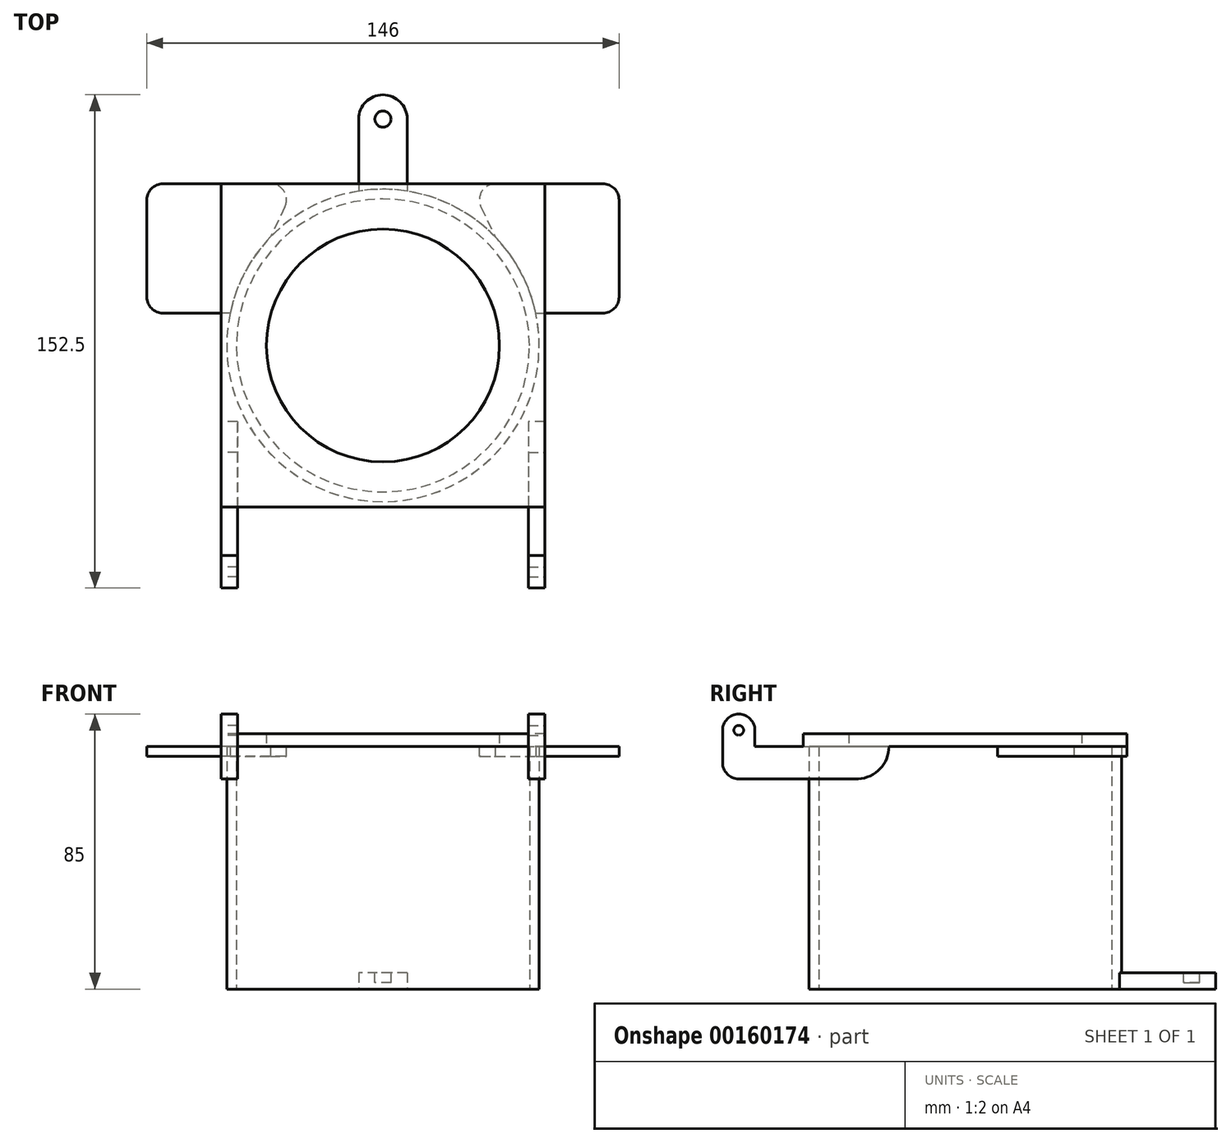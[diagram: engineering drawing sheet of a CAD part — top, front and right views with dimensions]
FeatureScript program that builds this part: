
annotation { "Feature Type Name" : "Feature", "Feature Type Description" : "" }
export const myFeature = defineFeature(function(context is Context, id is Id, definition is map)
    precondition{}
    {
        {
            var Q0;
            Q0=qCreatedBy(makeId("Top.planeOp"),FACE);
            var sketch = newSketch(context, id + "F0", { "sketchPlane" : qUnion([Q0])});
            skCircle(sketch, "E0", {"center": v(0, 0) * mm, "radius": 48.3 * mm});
            skCircle(sketch, "E1", {"center": v(0, 0) * mm, "radius": 45.3 * mm});
            skLineSegment(sketch, "E2.top", {"start": v(7.5, 46.67) * mm, "end": v(-7.5, 46.67) * mm});
            skLineSegment(sketch, "E2.left", {"start": v(7.5, 70) * mm, "end": v(7.5, 46.67) * mm});
            skLineSegment(sketch, "E2.right", {"start": v(-7.5, 70) * mm, "end": v(-7.5, 46.67) * mm});
            skArc(sketch, "E3", {"start": v(-7.5, 70) * mm, "mid": v(0, 77.5) * mm, "end": v(7.5, 70) * mm});
            skSolve(sketch);
        }
        {
            var Q0;
            Q0=makeQuery(id+"F0.imprint","IMPRINT",FACE,{"disambiguationData":[TD([[makeQuery(id+"F0.imprint","IMPRINT",EDGE,{"derivedFrom":sQuery(id+"F0.wireOp",EDGE,"E1")}),-1.0]])]});
            var Q1;
            {var subQ5=sQuery(id+"F0.wireOp",EDGE,"E2.top");Q1=makeQuery(id+"F0.imprint","IMPRINT",FACE,{"disambiguationData":[TD([[makeQuery(id+"F0.imprint","IMPRINT",EDGE,{"derivedFrom":subQ5}),-1.0]])]});}
            extrude(context, id + "F1", {"entities" : qUnion([Q0, Q1]), "depth" : 75 * mm});
        }
        {
            var Q0;
            Q0=qSketchRegion(id+"F0",true);
            extrude(context, id + "F2", {"entities" : qUnion([Q0]), "operationType" : NewBodyOperationType.ADD, "depth" : 5 * mm});
        }
        {
            var Q0;
            Q0=makeQuery(id+"F2.opExtrude","CAP_FACE",FACE,{"disambiguationData":[OSD([sQuery(id+"F0.wireOp",EDGE,"E0"),sQuery(id+"F0.wireOp",EDGE,"E1"),sQuery(id+"F0.wireOp",EDGE,"E2.left"),sQuery(id+"F0.wireOp",EDGE,"E2.right"),sQuery(id+"F0.wireOp",EDGE,"E3")])],"isStart":false});
            var sketch = newSketch(context, id + "F3", { "sketchPlane" : qUnion([Q0])});
            skCircle(sketch, "E4", {"center": v(0, 70) * mm, "radius": 2.5 * mm});
            skSolve(sketch);
        }
        {
            var Q0;
            Q0=makeQuery(id+"F3.imprint","IMPRINT",FACE,{"disambiguationData":[TD([[makeQuery(id+"F3.imprint","IMPRINT",EDGE,{"derivedFrom":sQuery(id+"F3.wireOp",EDGE,"E4")}),1.0]])]});
            extrude(context, id + "F4", {"entities" : qUnion([Q0]), "operationType" : NewBodyOperationType.REMOVE, "oppositeDirection" : true, "depth" : 3 * mm});
        }
        {
            var Q0;
            Q0=makeQuery(id+"F1.opExtrude","CAP_FACE",FACE,{"disambiguationData":[OSD([sQuery(id+"F0.wireOp",EDGE,"E0"),sQuery(id+"F0.wireOp",EDGE,"E1")])],"isStart":false});
            var sketch = newSketch(context, id + "F5", { "sketchPlane" : qUnion([Q0])});
            skLineSegment(sketch, "E5.bottom", {"start": v(50, 50) * mm, "end": v(-50, 50) * mm});
            skLineSegment(sketch, "E5.top", {"start": v(50, -50) * mm, "end": v(-50, -50) * mm});
            skLineSegment(sketch, "E5.left", {"start": v(50, 50) * mm, "end": v(50, -50) * mm});
            skLineSegment(sketch, "E5.right", {"start": v(-50, 50) * mm, "end": v(-50, -50) * mm});
            skPoint(sketch, "E5.middle", {"position": v(0, 0) * mm});
            skCircle(sketch, "E6", {"center": v(0, 0) * mm, "radius": 36 * mm});
            skSolve(sketch);
        }
        {
            var Q0;
            Q0=makeQuery(id+"F5.imprint","IMPRINT",FACE,{"disambiguationData":[TD([[makeQuery(id+"F5.imprint","IMPRINT",EDGE,{"derivedFrom":sQuery(id+"F5.wireOp",EDGE,"E6")}),-1.0]])]});
            var Q1;
            Q1=makeQuery(id+"F5.imprint","IMPRINT",FACE,{"disambiguationData":[TD([[makeQuery(id+"F5.imprint","IMPRINT",EDGE,{"derivedFrom":makeQuery(id+"F1.opExtrude","CAP_EDGE",EDGE,{"disambiguationData":[OSD([sQuery(id+"F0.wireOp",EDGE,"E0")])],"isStart":false})}),1.0]])]});
            var Q2;
            Q2=makeQuery(id+"F5.imprint","IMPRINT",FACE,{"disambiguationData":[TD([[makeQuery(id+"F5.imprint","IMPRINT",EDGE,{"derivedFrom":sQuery(id+"F5.wireOp",EDGE,"E5.bottom")}),1.0]])]});
            extrude(context, id + "F6", {"entities" : qUnion([Q0, Q1, Q2]), "operationType" : NewBodyOperationType.ADD, "depth" : 4 * mm});
        }
        {
            var Q0;
            Q0=makeQuery(id+"F6.opExtrude","CAP_FACE",FACE,{"disambiguationData":[OSD([sQuery(id+"F5.wireOp",EDGE,"E5.bottom"),sQuery(id+"F5.wireOp",EDGE,"E5.top"),sQuery(id+"F5.wireOp",EDGE,"E5.left"),sQuery(id+"F5.wireOp",EDGE,"E5.right"),sQuery(id+"F5.wireOp",EDGE,"E6")])],"isStart":true});
            var sketch = newSketch(context, id + "F7", { "sketchPlane" : qUnion([Q0])});
            skLineSegment(sketch, "E7.bottom", {"start": v(-45.94, -50) * mm, "end": v(-68, -50) * mm});
            skLineSegment(sketch, "E7.top", {"start": v(-45.94, -10) * mm, "end": v(-68, -10) * mm});
            skLineSegment(sketch, "E7.right", {"start": v(-73, -45) * mm, "end": v(-73, -15) * mm});
            skPoint(sketch, "E8", {"position": v(-50, -10) * mm});
            skPoint(sketch, "E9", {"position": v(-50, -50) * mm});
            skLineSegment(sketch, "E10", {"start": v(-45.94, -50) * mm, "end": v(-34.82, -50) * mm});
            skLineSegment(sketch, "E11", {"start": v(-30.3, -42.85) * mm, "end": v(-45.94, -10) * mm});
            skPoint(sketch, "E12.visualSharp", {"position": v(-73, -10) * mm});
            skArc(sketch, "E12.filletArc", {"start": v(-68, -10) * mm, "mid": v(-71.54, -11.46) * mm, "end": v(-73, -15) * mm});
            skPoint(sketch, "E13.visualSharp", {"position": v(-73, -50) * mm});
            skArc(sketch, "E13.filletArc", {"start": v(-73, -45) * mm, "mid": v(-71.54, -48.54) * mm, "end": v(-68, -50) * mm});
            skLineSegment(sketch, "E14.MirrorCS", {"start": v(45.94, -10) * mm, "end": v(68, -10) * mm});
            skLineSegment(sketch, "E15.MirrorCS", {"start": v(30.3, -42.85) * mm, "end": v(45.94, -10) * mm});
            skLineSegment(sketch, "E16.MirrorCS", {"start": v(45.94, -50) * mm, "end": v(34.82, -50) * mm});
            skLineSegment(sketch, "E17.MirrorCS", {"start": v(45.94, -50) * mm, "end": v(68, -50) * mm});
            skArc(sketch, "E18.MirrorCS", {"start": v(73, -45) * mm, "mid": v(71.54, -48.54) * mm, "end": v(68, -50) * mm});
            skLineSegment(sketch, "E19.MirrorCS", {"start": v(73, -45) * mm, "end": v(73, -15) * mm});
            skArc(sketch, "E20.MirrorCS", {"start": v(68, -10) * mm, "mid": v(71.54, -11.46) * mm, "end": v(73, -15) * mm});
            skPoint(sketch, "E21.visualSharp", {"position": v(-26.9, -50) * mm});
            skArc(sketch, "E21.filletArc", {"start": v(-34.82, -50) * mm, "mid": v(-30.6, -47.67) * mm, "end": v(-30.3, -42.85) * mm});
            skPoint(sketch, "E22.visualSharp", {"position": v(26.9, -50) * mm});
            skArc(sketch, "E22.filletArc", {"start": v(30.3, -42.85) * mm, "mid": v(30.6, -47.67) * mm, "end": v(34.82, -50) * mm});
            skSolve(sketch);
        }
        {
            var Q0;
            Q0 = qSketchRegion(id + "F7", true);
            extrude(context, id + "F8", {"entities" : qUnion([Q0]), "operationType" : NewBodyOperationType.ADD, "depth" : 3 * mm});
        }
        {
            var Q0;
            {var subQ0=sQuery(id+"F5.wireOp",EDGE,"E5.right");var subQ3=sQuery(id+"F5.wireOp",EDGE,"E5.left");var subQ6=sQuery(id+"F5.wireOp",EDGE,"E5.top");var subQ7=makeQuery(id+"F6.opExtrude","SWEPT_FACE",FACE,{"disambiguationData":[OSD([subQ6])]});var subQ8=makeQuery(id+"F1.opExtrude","SWEPT_FACE",FACE,{"disambiguationData":[OSD([sQuery(id+"F0.wireOp",EDGE,"E0")])]});var subQ9=sQuery(id+"F5.wireOp",EDGE,"E5.bottom");Q0=makeQuery(id+"F8.boolean.opBoolean","SPLIT",FACE,{"disambiguationData":[TD([subQ7])],"derivedFrom":makeQuery(id+"F6.boolean.opBoolean","SPLIT",FACE,{"disambiguationData":[TD([subQ8])],"derivedFrom":makeQuery(id+"F6.opExtrude","CAP_FACE",FACE,{"disambiguationData":[OSD([subQ9,subQ6,subQ3,subQ0,sQuery(id+"F5.wireOp",EDGE,"E6")])],"isStart":true})})});}
            var sketch = newSketch(context, id + "F9", { "sketchPlane" : qUnion([Q0])});
            skLineSegment(sketch, "E23.bottom", {"start": v(50, 23.56) * mm, "end": v(45, 23.56) * mm});
            skLineSegment(sketch, "E23.top", {"start": v(50, 70) * mm, "end": v(45, 70) * mm});
            skLineSegment(sketch, "E23.left", {"start": v(50, 23.56) * mm, "end": v(50, 70) * mm});
            skLineSegment(sketch, "E23.right", {"start": v(45, 23.56) * mm, "end": v(45, 70) * mm});
            skPoint(sketch, "E24", {"position": v(50, 50) * mm});
            skSolve(sketch);
        }
        {
            var Q0;
            {var subQ0=sQuery(id+"F9.wireOp",EDGE,"E23.bottom");Q0=makeQuery(id+"F9.imprint","IMPRINT",FACE,{"disambiguationData":[TD([[makeQuery(id+"F9.imprint","IMPRINT",EDGE,{"derivedFrom":subQ0}),-1.0]])]});}
            var Q1;
            {var subQ0=sQuery(id+"F9.wireOp",EDGE,"E23.top");Q1=makeQuery(id+"F9.imprint","IMPRINT",FACE,{"disambiguationData":[TD([[makeQuery(id+"F9.imprint","IMPRINT",EDGE,{"derivedFrom":subQ0}),1.0]])]});}
            extrude(context, id + "F10", {"entities" : qUnion([Q0, Q1]), "operationType" : NewBodyOperationType.ADD, "depth" : 10 * mm});
        }
        {
            var Q0;
            Q0=makeQuery(id+"F10.boolean.opBoolean","MERGE",FACE,{"derivedFrom":[makeQuery(id+"F6.opExtrude","SWEPT_FACE",FACE,{"disambiguationData":[OSD([sQuery(id+"F5.wireOp",EDGE,"E5.left")])]}),makeQuery(id+"F10.opExtrude","SWEPT_FACE",FACE,{"disambiguationData":[OSD([sQuery(id+"F9.wireOp",EDGE,"E23.left")])]})]});
            var sketch = newSketch(context, id + "F11", { "sketchPlane" : qUnion([Q0])});
            skArc(sketch, "E25", {"start": v(-33.08, 65) * mm, "mid": v(-26.32, 68.1) * mm, "end": v(-23.56, 75) * mm});
            skLineSegment(sketch, "E26.bottom", {"start": v(-50, 75) * mm, "end": v(-70, 75) * mm});
            skLineSegment(sketch, "E26.left", {"start": v(-50, 75) * mm, "end": v(-50, 79) * mm});
            skSolve(sketch);
        }
        {
            var Q0;
            {var subQ0=sQuery(id+"F11.wireOp",EDGE,"E25");Q0=makeQuery(id+"F11.imprint","IMPRINT",FACE,{"disambiguationData":[TD([[makeQuery(id+"F11.imprint","IMPRINT",EDGE,{"derivedFrom":subQ0}),-1.0]])]});}
            extrude(context, id + "F12", {"entities" : qUnion([Q0]), "operationType" : NewBodyOperationType.REMOVE, "endBound" : BoundingType.UP_TO_NEXT, "oppositeDirection" : true, "depth" : 25 * mm});
        }
        {
            var Q0;
            Q0=makeQuery(id+"F10.boolean.opBoolean","MERGE",FACE,{"derivedFrom":[makeQuery(id+"F6.opExtrude","SWEPT_FACE",FACE,{"disambiguationData":[OSD([sQuery(id+"F5.wireOp",EDGE,"E5.left")])]}),makeQuery(id+"F10.opExtrude","SWEPT_FACE",FACE,{"disambiguationData":[OSD([sQuery(id+"F9.wireOp",EDGE,"E23.left")])]})]});
            var sketch = newSketch(context, id + "F13", { "sketchPlane" : qUnion([Q0])});
            skLineSegment(sketch, "E27", {"start": v(-70, 75) * mm, "end": v(-65, 75) * mm});
            skLineSegment(sketch, "E28", {"start": v(-65, 75) * mm, "end": v(-65, 85) * mm});
            skLineSegment(sketch, "E29", {"start": v(-65, 85) * mm, "end": v(-75, 85) * mm});
            skLineSegment(sketch, "E30", {"start": v(-75, 85) * mm, "end": v(-75, 65) * mm});
            skLineSegment(sketch, "E31", {"start": v(-75, 65) * mm, "end": v(-70, 65) * mm});
            skLineSegment(sketch, "E32", {"start": v(-70, 65) * mm, "end": v(-75, 65) * mm});
            skSolve(sketch);
        }
        {
            var Q0;
            Q0=makeQuery(id+"F13.imprint","IMPRINT",FACE,{"disambiguationData":[TD([[makeQuery(id+"F13.imprint","IMPRINT",EDGE,{"derivedFrom":sQuery(id+"F13.wireOp",EDGE,"E27")}),-1.0]])]});
            extrude(context, id + "F14", {"entities" : qUnion([Q0]), "operationType" : NewBodyOperationType.ADD, "oppositeDirection" : true, "depth" : 5 * mm});
        }
        {
            var Q0;
            Q0=makeQuery(id+"F14.opExtrude","SWEPT_EDGE",EDGE,{"disambiguationData":[OSD([sQuery(id+"F13.wireOp",EDGE,"E30"),sQuery(id+"F13.wireOp",EDGE,"E32")])]});
            fillet(context, id + "F15", {"entities" : qUnion([Q0]), "radius" : 5 * mm, "tangentPropagation" : true, "allowEdgeOverflow" : false});
        }
        {
            var Q0;
            Q0=makeQuery(id+"F14.opExtrude","SWEPT_EDGE",EDGE,{"disambiguationData":[OSD([sQuery(id+"F13.wireOp",EDGE,"E29"),sQuery(id+"F13.wireOp",EDGE,"E30")])]});
            var Q1;
            Q1=makeQuery(id+"F14.opExtrude","SWEPT_EDGE",EDGE,{"disambiguationData":[OSD([sQuery(id+"F13.wireOp",EDGE,"E28"),sQuery(id+"F13.wireOp",EDGE,"E29")])]});
            fillet(context, id + "F16", {"entities" : qUnion([Q0, Q1]), "radius" : 5 * mm, "tangentPropagation" : true, "allowEdgeOverflow" : false});
        }
        {
            var Q0;
            {var subQ0=sQuery(id+"F9.wireOp",EDGE,"E23.left");Q0=makeQuery(id+"F14.boolean.opBoolean","MERGE",FACE,{"derivedFrom":[makeQuery(id+"F10.boolean.opBoolean","MERGE",FACE,{"derivedFrom":[makeQuery(id+"F6.opExtrude","SWEPT_FACE",FACE,{"disambiguationData":[OSD([sQuery(id+"F5.wireOp",EDGE,"E5.left")])]}),makeQuery(id+"F10.opExtrude","SWEPT_FACE",FACE,{"disambiguationData":[OSD([subQ0])]})]}),makeQuery(id+"F14.opExtrude","CAP_FACE",FACE,{"disambiguationData":[OSD([sQuery(id+"F9.wireOp",EDGE,"E23.top"),subQ0,sQuery(id+"F13.wireOp",EDGE,"E27"),sQuery(id+"F13.wireOp",EDGE,"E28"),sQuery(id+"F13.wireOp",EDGE,"E29"),sQuery(id+"F13.wireOp",EDGE,"E30"),sQuery(id+"F13.wireOp",EDGE,"E32")])],"isStart":true})]});}
            var sketch = newSketch(context, id + "F17", { "sketchPlane" : qUnion([Q0])});
            skPoint(sketch, "E33", {"position": v(-70, 80) * mm});
            skCircle(sketch, "E34", {"center": v(-70, 80) * mm, "radius": 1.5 * mm});
            skSolve(sketch);
        }
        {
            var Q0;
            Q0 = qSketchRegion(id + "F17", true);
            extrude(context, id + "F18", {"entities" : qUnion([Q0]), "operationType" : NewBodyOperationType.REMOVE, "endBound" : BoundingType.UP_TO_NEXT, "oppositeDirection" : true, "depth" : 25 * mm});
        }
        {
            var Q0;
            Q0=makeQuery(id+"F6.opExtrude","SWEPT_FACE",FACE,{"disambiguationData":[OSD([sQuery(id+"F5.wireOp",EDGE,"E5.right")])]});
            cPlane(context, id + "F19", {"entities" : qUnion([Q0]), "cplaneType" : CPlaneType.OFFSET, "offset" : 0 * mm, "width" : 150 * mm, "height" : 150 * mm});
        }
        {
            var Q0;
            Q0=qCreatedBy(id+"F19.planeOp",FACE);
            var sketch = newSketch(context, id + "F20", { "sketchPlane" : qUnion([Q0])});
            skArc(sketch, "E35.0.0", {"start": v(75, 80) * mm, "mid": v(70, 85) * mm, "end": v(65, 80) * mm});
            skLineSegment(sketch, "E35.0.1", {"start": v(65, 80) * mm, "end": v(65, 75) * mm});
            skLineSegment(sketch, "E35.0.2", {"start": v(65, 75) * mm, "end": v(50, 75) * mm});
            skLineSegment(sketch, "E35.0.3", {"start": v(50, 75) * mm, "end": v(23.56, 75) * mm});
            skArc(sketch, "E35.0.4", {"start": v(33.08, 65) * mm, "mid": v(26.32, 68.1) * mm, "end": v(23.56, 75) * mm});
            skLineSegment(sketch, "E35.0.5", {"start": v(33.08, 65) * mm, "end": v(70, 65) * mm});
            skArc(sketch, "E35.0.6", {"start": v(70, 65) * mm, "mid": v(73.54, 66.46) * mm, "end": v(75, 70) * mm});
            skLineSegment(sketch, "E35.0.7", {"start": v(75, 70) * mm, "end": v(75, 80) * mm});
            skCircle(sketch, "E36.0", {"center": v(70, 80) * mm, "radius": 1.5 * mm});
            skSolve(sketch);
        }
        {
            var Q0;
            Q0=makeQuery(id+"F20.imprint","IMPRINT",FACE,{"disambiguationData":[TD([[makeQuery(id+"F20.imprint","IMPRINT",EDGE,{"derivedFrom":sQuery(id+"F20.wireOp",EDGE,"E35.0.0")}),1.0]])]});
            extrude(context, id + "F21", {"entities" : qUnion([Q0]), "operationType" : NewBodyOperationType.ADD, "oppositeDirection" : true, "depth" : 5 * mm});
        }
    });
